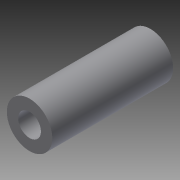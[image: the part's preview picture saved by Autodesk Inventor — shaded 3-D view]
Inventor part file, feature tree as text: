
AUTODESK INVENTOR PART (.ipt)
format: ipt  version: 2014 SP2 (Build 180246200, 246)  size: 97,792 bytes
history: native  units: in
note: dims shown in document units (in); Inventor stores cm internally (conversion verified against a paired STEP export)
features: other x7, sketch x2, revolve x1, hole x1
ambient origin geometry x8: Origin, YZ Plane, XZ Plane, XY Plane, X Axis, Y Axis, Z Axis, Center Point
bodies: Solid1 (feature_tree)
feature tree (11):
  revolve  "Revolution1"  [1 undecoded]
  hole  "Hole1"  [1 undecoded]
  other  "screw_XY"
  other  "screw_YZ"
  other  "screw_ZX"
  other  "screw_X"
  other  "screw_Y"
  other  "screw_Z"
  other  "screw_Center"
  sketch  "Sketch_1"  dims[d0=360.0deg]
  sketch  "Sketch2"  dims[d1=0.118in d2=0.75in d3=0.375in d4=0.25in d5=0.5635in d6=0.625in d7=0.0in d8=0.0in]
note: 2 required parameter values undecoded (feature->parameter linkage not recoverable at this tier; creation-order binding heuristic only, values carry confidence <= 0.55)